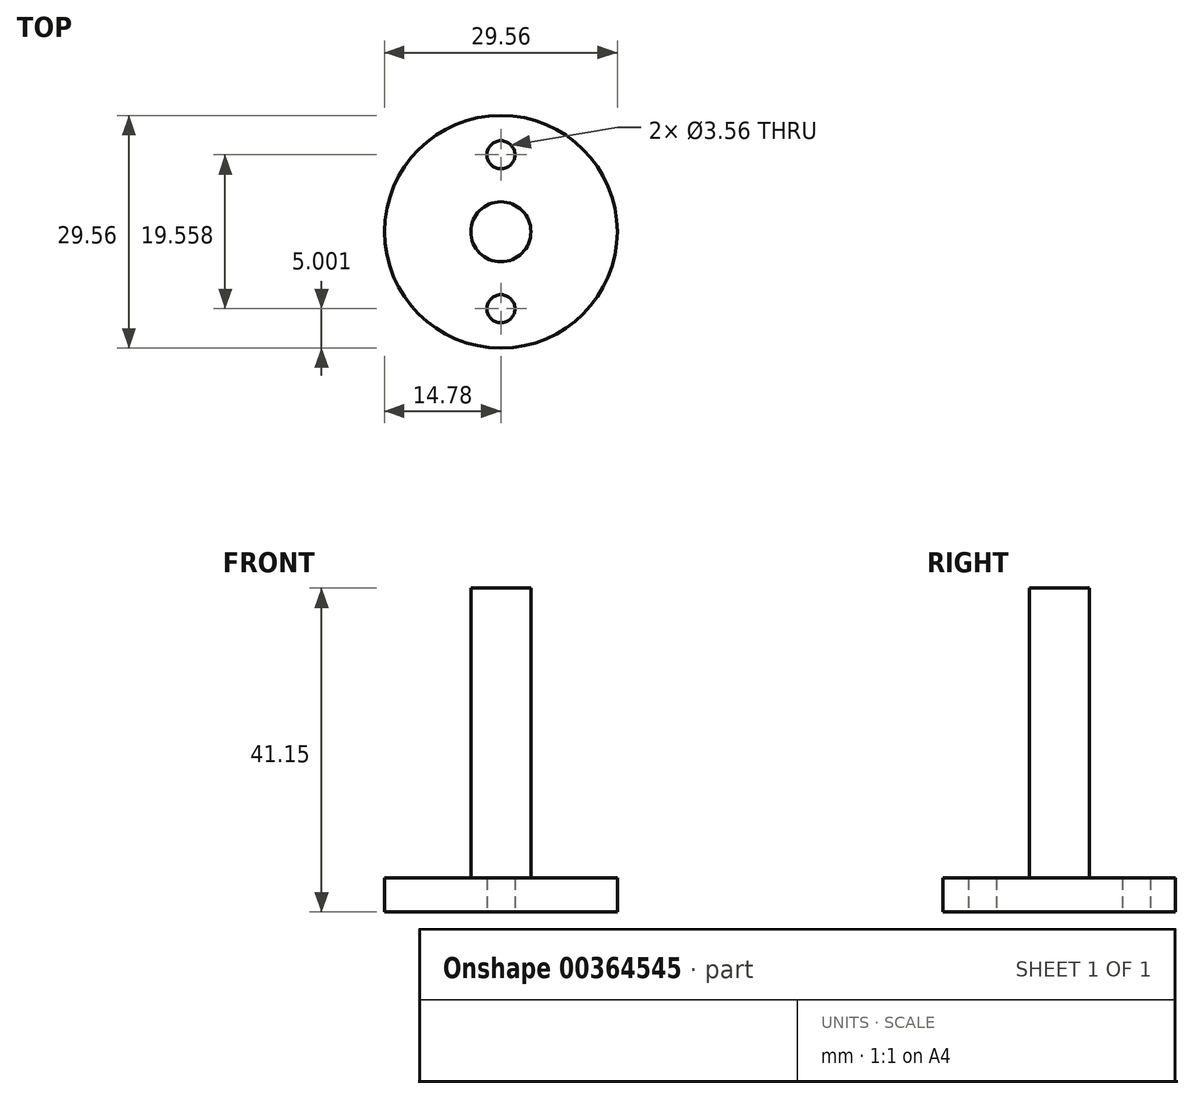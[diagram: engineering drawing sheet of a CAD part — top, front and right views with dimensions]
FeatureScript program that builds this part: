
annotation { "Feature Type Name" : "Feature", "Feature Type Description" : "" }
export const myFeature = defineFeature(function(context is Context, id is Id, definition is map)
    precondition{}
    {
        {
            var Q0;
            Q0=qCreatedBy(makeId("Top.planeOp"),FACE);
            var sketch = newSketch(context, id + "F0", { "sketchPlane" : qUnion([Q0])});
            skCircle(sketch, "E0", {"center": v(0, 9.78) * mm, "radius": 1.78 * mm});
            skCircle(sketch, "E1", {"center": v(0, -9.78) * mm, "radius": 1.78 * mm});
            skCircle(sketch, "E2", {"center": v(0, 0) * mm, "radius": 14.78 * mm});
            skSolve(sketch);
        }
        {
            var Q0;
            Q0=makeQuery(id+"F0.imprint","IMPRINT",FACE,{"disambiguationData":[TD([[makeQuery(id+"F0.imprint","IMPRINT",EDGE,{"derivedFrom":sQuery(id+"F0.wireOp",EDGE,"E0")}),-1.0]])]});
            extrude(context, id + "F1", {"entities" : qUnion([Q0]), "depth" : 4.32 * mm});
        }
        {
            var Q0;
            Q0=makeQuery(id+"F1.opExtrude","CAP_FACE",FACE,{"disambiguationData":[OSD([sQuery(id+"F0.wireOp",EDGE,"E0"),sQuery(id+"F0.wireOp",EDGE,"E1"),sQuery(id+"F0.wireOp",EDGE,"E2")])],"isStart":false});
            var sketch = newSketch(context, id + "F2", { "sketchPlane" : qUnion([Q0])});
            skCircle(sketch, "E3", {"center": v(0, 0) * mm, "radius": 3.81 * mm});
            skSolve(sketch);
        }
        {
            var Q0;
            Q0=makeQuery(id+"F2.imprint","IMPRINT",FACE,{"disambiguationData":[TD([[makeQuery(id+"F2.imprint","IMPRINT",EDGE,{"derivedFrom":sQuery(id+"F2.wireOp",EDGE,"E3")}),1.0]])]});
            extrude(context, id + "F3", {"entities" : qUnion([Q0]), "operationType" : NewBodyOperationType.ADD, "depth" : 36.83 * mm});
        }
    });
